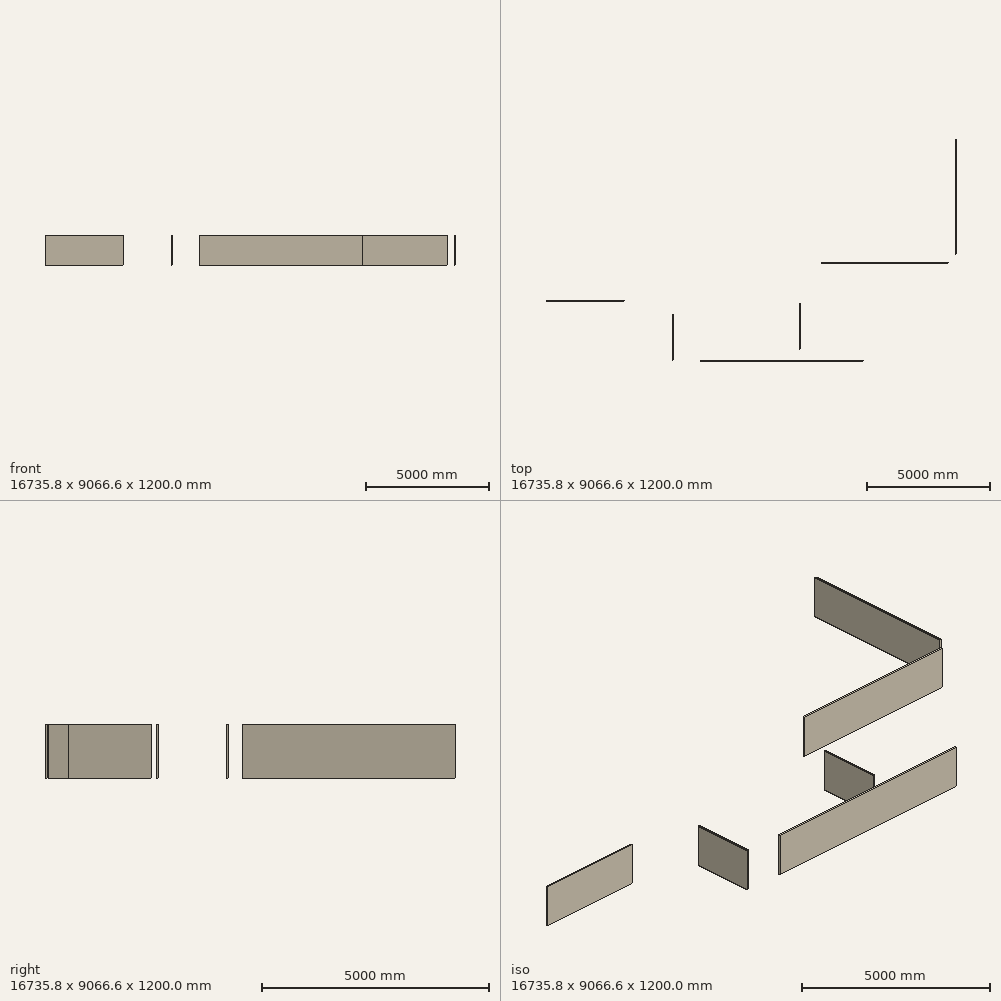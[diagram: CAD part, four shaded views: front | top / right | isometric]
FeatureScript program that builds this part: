
annotation { "Feature Type Name" : "Feature", "Feature Type Description" : "" }
export const myFeature = defineFeature(function(context is Context, id is Id, definition is map)
    precondition{}
    {
        {
            var Q0;
            Q0=qCreatedBy(makeId("Top.planeOp"),FACE);
            var sketch = newSketch(context, id + "F0", { "sketchPlane" : qUnion([Q0])});
            skLineSegment(sketch, "E0.bottom", {"start": v(60.88, 4666.89) * mm, "end": v(110.88, 4666.89) * mm});
            skLineSegment(sketch, "E0.top", {"start": v(60.88, -33.11) * mm, "end": v(110.88, -33.11) * mm});
            skLineSegment(sketch, "E0.left", {"start": v(60.88, 4666.89) * mm, "end": v(60.88, -33.11) * mm});
            skLineSegment(sketch, "E0.right", {"start": v(110.88, 4666.89) * mm, "end": v(110.88, -33.11) * mm});
            skLineSegment(sketch, "E1.bottom", {"start": v(-198.82, -396.04) * mm, "end": v(-5398.82, -396.04) * mm});
            skLineSegment(sketch, "E1.top", {"start": v(-198.82, -346.04) * mm, "end": v(-5398.82, -346.04) * mm});
            skLineSegment(sketch, "E1.left", {"start": v(-198.82, -396.04) * mm, "end": v(-198.82, -346.04) * mm});
            skLineSegment(sketch, "E1.right", {"start": v(-5398.82, -396.04) * mm, "end": v(-5398.82, -346.04) * mm});
            skLineSegment(sketch, "E2.bottom", {"start": v(-6243.09, -2045.63) * mm, "end": v(-6293.09, -2045.63) * mm});
            skLineSegment(sketch, "E2.top", {"start": v(-6243.09, -3895.63) * mm, "end": v(-6293.09, -3895.63) * mm});
            skLineSegment(sketch, "E2.left", {"start": v(-6243.09, -2045.63) * mm, "end": v(-6243.09, -3895.63) * mm});
            skLineSegment(sketch, "E2.right", {"start": v(-6293.09, -2045.63) * mm, "end": v(-6293.09, -3895.63) * mm});
            skLineSegment(sketch, "E3.bottom", {"start": v(-3671.94, -4399.71) * mm, "end": v(-10321.94, -4399.71) * mm});
            skLineSegment(sketch, "E3.top", {"start": v(-3671.94, -4349.71) * mm, "end": v(-10321.94, -4349.71) * mm});
            skLineSegment(sketch, "E3.left", {"start": v(-3671.94, -4399.71) * mm, "end": v(-3671.94, -4349.71) * mm});
            skLineSegment(sketch, "E3.right", {"start": v(-10321.94, -4399.71) * mm, "end": v(-10321.94, -4349.71) * mm});
            skLineSegment(sketch, "E4.bottom", {"start": v(-11451.4, -4342.23) * mm, "end": v(-11501.4, -4342.23) * mm});
            skLineSegment(sketch, "E4.top", {"start": v(-11451.4, -2492.23) * mm, "end": v(-11501.4, -2492.23) * mm});
            skLineSegment(sketch, "E4.left", {"start": v(-11451.4, -4342.23) * mm, "end": v(-11451.4, -2492.23) * mm});
            skLineSegment(sketch, "E4.right", {"start": v(-11501.4, -4342.23) * mm, "end": v(-11501.4, -2492.23) * mm});
            skLineSegment(sketch, "E5.bottom", {"start": v(-13424.96, -1903.08) * mm, "end": v(-16624.96, -1903.08) * mm});
            skLineSegment(sketch, "E5.top", {"start": v(-13424.96, -1953.08) * mm, "end": v(-16624.96, -1953.08) * mm});
            skLineSegment(sketch, "E5.left", {"start": v(-13424.96, -1903.08) * mm, "end": v(-13424.96, -1953.08) * mm});
            skLineSegment(sketch, "E5.right", {"start": v(-16624.96, -1903.08) * mm, "end": v(-16624.96, -1953.08) * mm});
            skSolve(sketch);
        }
        {
            var Q0;
            Q0=makeQuery(id+"F0.imprint","IMPRINT",FACE,{"disambiguationData":[TD([[makeQuery(id+"F0.imprint","IMPRINT",EDGE,{"derivedFrom":sQuery(id+"F0.wireOp",EDGE,"E0.bottom")}),-1.0]])]});
            var Q1;
            Q1=makeQuery(id+"F0.imprint","IMPRINT",FACE,{"disambiguationData":[TD([[makeQuery(id+"F0.imprint","IMPRINT",EDGE,{"derivedFrom":sQuery(id+"F0.wireOp",EDGE,"E1.bottom")}),-1.0]])]});
            var Q2;
            Q2=makeQuery(id+"F0.imprint","IMPRINT",FACE,{"disambiguationData":[TD([[makeQuery(id+"F0.imprint","IMPRINT",EDGE,{"derivedFrom":sQuery(id+"F0.wireOp",EDGE,"E2.bottom")}),1.0]])]});
            var Q3;
            Q3=makeQuery(id+"F0.imprint","IMPRINT",FACE,{"disambiguationData":[TD([[makeQuery(id+"F0.imprint","IMPRINT",EDGE,{"derivedFrom":sQuery(id+"F0.wireOp",EDGE,"E3.bottom")}),-1.0]])]});
            var Q4;
            Q4=makeQuery(id+"F0.imprint","IMPRINT",FACE,{"disambiguationData":[TD([[makeQuery(id+"F0.imprint","IMPRINT",EDGE,{"derivedFrom":sQuery(id+"F0.wireOp",EDGE,"E4.bottom")}),-1.0]])]});
            var Q5;
            Q5=makeQuery(id+"F0.imprint","IMPRINT",FACE,{"disambiguationData":[TD([[makeQuery(id+"F0.imprint","IMPRINT",EDGE,{"derivedFrom":sQuery(id+"F0.wireOp",EDGE,"E5.bottom")}),1.0]])]});
            extrude(context, id + "F1", {"entities" : qUnion([Q0, Q1, Q2, Q3, Q4, Q5]), "depth" : 1200 * mm, "offsetDistance" : 25 * mm});
        }
    });
